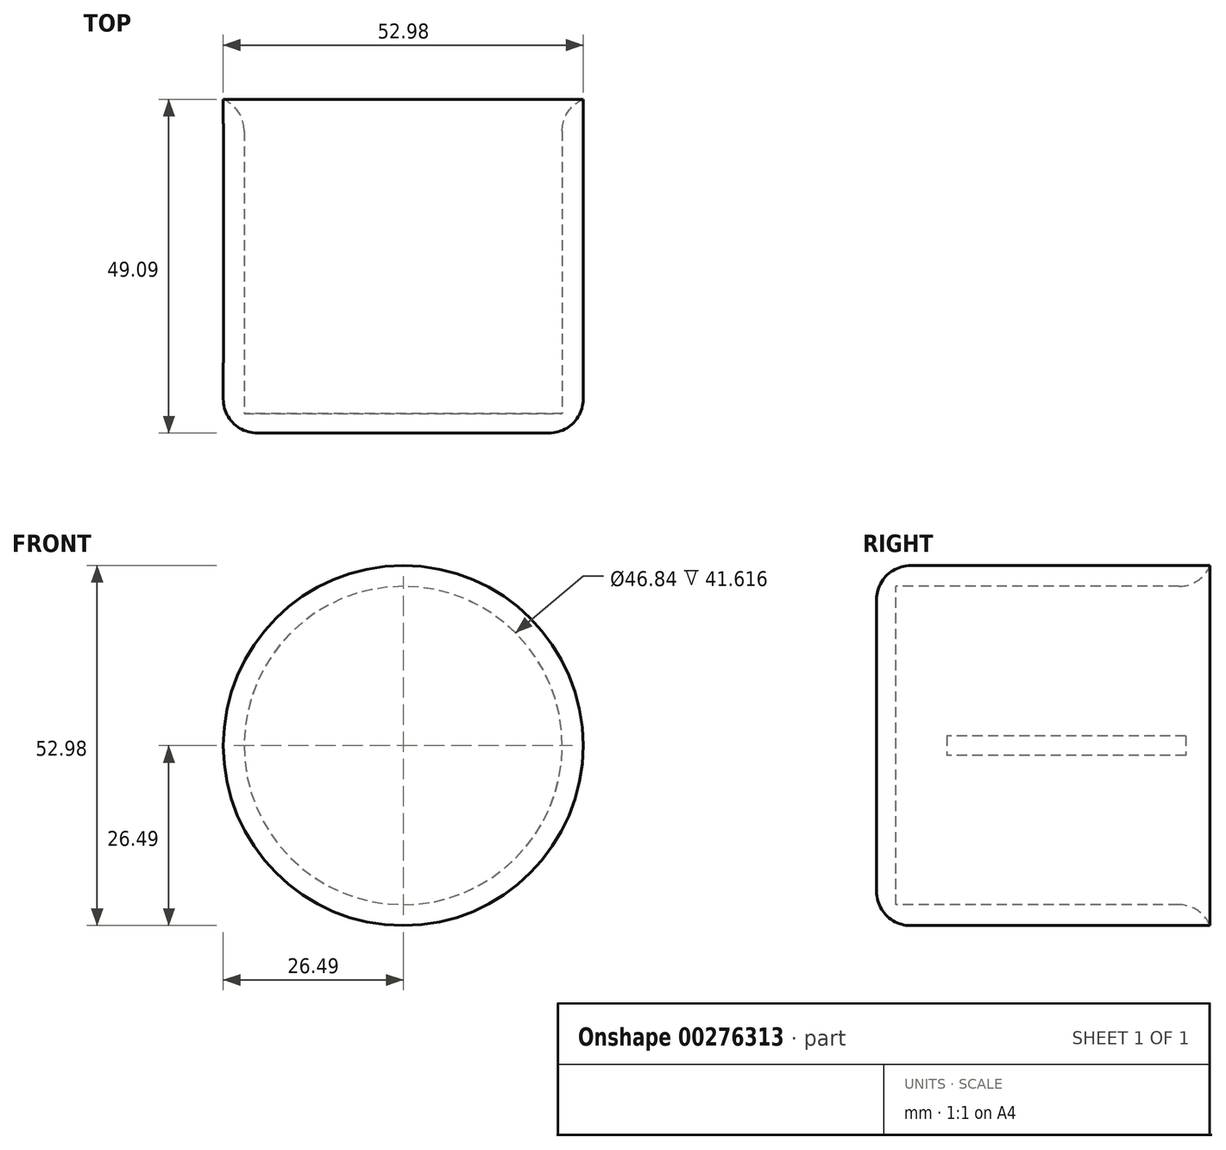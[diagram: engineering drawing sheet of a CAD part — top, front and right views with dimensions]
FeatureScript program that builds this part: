
annotation { "Feature Type Name" : "Feature", "Feature Type Description" : "" }
export const myFeature = defineFeature(function(context is Context, id is Id, definition is map)
    precondition{}
    {
        {
            var Q0;
            Q0=qCreatedBy(makeId("Top.planeOp"),FACE);
            var sketch = newSketch(context, id + "F0", { "sketchPlane" : qUnion([Q0])});
            skLineSegment(sketch, "E0.bottom", {"start": v(-26.49, 28.64) * mm, "end": v(-23.42, 28.64) * mm});
            skLineSegment(sketch, "E0.top", {"start": v(-26.49, -20.45) * mm, "end": v(-23.42, -20.45) * mm});
            skLineSegment(sketch, "E0.left", {"start": v(-26.49, 28.64) * mm, "end": v(-26.49, -20.45) * mm});
            skLineSegment(sketch, "E0.right", {"start": v(-23.42, 28.64) * mm, "end": v(-23.42, -20.45) * mm});
            skLineSegment(sketch, "E1.bottom", {"start": v(-23.42, -20.45) * mm, "end": v(0, -20.45) * mm});
            skLineSegment(sketch, "E1.top", {"start": v(-23.42, -17.6) * mm, "end": v(0, -17.6) * mm});
            skLineSegment(sketch, "E1.left", {"start": v(-23.42, -20.45) * mm, "end": v(-23.42, -17.6) * mm});
            skLineSegment(sketch, "E1.right", {"start": v(0, -20.45) * mm, "end": v(0, -17.6) * mm});
            skSolve(sketch);
        }
        {
            var Q0;
            Q0 = qSketchRegion(id + "F0", true);
            var Q1;
            Q1=sQuery(id+"F0.wireOp",EDGE,"E1.right");
            revolve(context, id + "F1", {"entities" : qUnion([Q0]), "axis" : qUnion([Q1]), "revolveType" : RevolveType.FULL});
        }
        {
            var Q0;
            Q0=qCreatedBy(makeId("Right.planeOp"),FACE);
            cPlane(context, id + "F2", {"entities" : qUnion([Q0]), "cplaneType" : CPlaneType.OFFSET, "offset" : 26.45 * mm, "oppositeDirection" : true, "width" : 150 * mm, "height" : 150 * mm});
        }
        {
            var Q0;
            Q0=makeQuery(id+"F1.opRevolve","SWEPT_EDGE",EDGE,{"disambiguationData":[OSD([sQuery(id+"F0.wireOp",EDGE,"E0.top"),sQuery(id+"F0.wireOp",EDGE,"E0.left")])]});
            fillet(context, id + "F3", {"entities" : qUnion([Q0]), "radius" : 5 * mm, "tangentPropagation" : true, "allowEdgeOverflow" : false});
        }
        {
            var Q0;
            Q0=makeQuery(id+"F1.opRevolve","SWEPT_EDGE",EDGE,{"disambiguationData":[OSD([sQuery(id+"F0.wireOp",EDGE,"E0.bottom"),sQuery(id+"F0.wireOp",EDGE,"E0.right")])]});
            fillet(context, id + "F4", {"entities" : qUnion([Q0]), "radius" : 5 * mm, "tangentPropagation" : true, "allowEdgeOverflow" : false});
        }
        {
            var Q0;
            Q0=qCreatedBy(id+"F2.planeOp",FACE);
            var sketch = newSketch(context, id + "F5", { "sketchPlane" : qUnion([Q0])});
            skLineSegment(sketch, "E2.bottom", {"start": v(25.06, 17.18) * mm, "end": v(-10.12, 17.18) * mm});
            skLineSegment(sketch, "E2.top", {"start": v(25.06, -19.23) * mm, "end": v(-10.12, -19.23) * mm});
            skLineSegment(sketch, "E2.left", {"start": v(25.06, 17.18) * mm, "end": v(25.06, -19.23) * mm});
            skLineSegment(sketch, "E2.right", {"start": v(-10.12, 17.18) * mm, "end": v(-10.12, -19.23) * mm});
            skSolve(sketch);
        }
        {
            var Q0;
            Q0=makeQuery(id+"F5.imprint","IMPRINT",FACE,{"disambiguationData":[TD([[makeQuery(id+"F5.imprint","IMPRINT",EDGE,{"derivedFrom":sQuery(id+"F5.wireOp",EDGE,"E2.bottom")}),1.0]])]});
            extrude(context, id + "F6", {"entities" : qUnion([Q0]), "operationType" : NewBodyOperationType.REMOVE, "oppositeDirection" : true, "depth" : 64 * mm});
        }
    });
